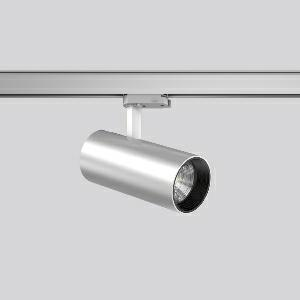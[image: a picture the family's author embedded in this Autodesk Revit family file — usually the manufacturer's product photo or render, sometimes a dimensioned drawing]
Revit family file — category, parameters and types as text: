
# Revit family: deecos_s_mini_742200_004_1_ad45
name_source: partatom
category: Lighting Fixtures
units: mm (PartAtom-declared; Revit-internal decimal feet)

## family parameters
Cut with Voids When Loaded = No
Host = Face
Light Source = No
Part Type = Normal
Room Calculation Point = No
Round Connector Dimension = Use Diameter
Shared = No

## types (1)
- DEECOS S mini (1 x LED Modul 940, 2150 lm, 4000)
    Apparent Load = 20 VA
    Approval mark = CE
    CIE Flux Codes = 98 100 100 100 100
    Color Rendering = 92
    Color Temperature = 4000
    Default Elevation = 1800 mm
    Description = Series: DEECOS S mini
LED surface-mounted projector in modern design with no visible cooling ribs. Housing: die-cast aluminium, powder-coated. Rotation range: 356°. Swivel range: 90°. Black plastic ring and recessed LED to prevent glare from the side. Optical assembly with lens made of plastic (polycarbonate) for the best homogeneous light distribution - can be changed without tools. Best colour rendering index Ra>90. With multi adaptor for 3-circuit tracks 230 V. Suitable for Track on ceiling, Wall track. High quality converter without flickering and stroboscopic effect. The following accessories can be mounted without use of tools: interchangeable lenses, decorative glasses, honeycomb louvre, clear and frosted diffusers, white interchangeable plastic ring. 
Colour: silver
Diameter: 87 mm
Height: 214 mm
Lamp: LED
Socket: without socket
Colour temperature: 4000K
Colour rendering index (CRI): 92
System power: 20 W
Rated luminous flux: 2150 lm
Luminous efficiency: 108 lm/W
Control gear: Regulated power supply
Protection class: I
Type of protection: IP 20
    Height = 214 mm
    Lamp = 1 x LED Modul 940
    Lamp Light Flux = 2150 lm
    Lamp count = 1
    Length = 87 mm
    Lifetime = 50000 h
    Luminous efficacy = 108 lm/W
    Manufacturer = RZB
    ModVariant = No
    Model = 742200.004.1
    Mounting Place = Ceiling
    Mounting Type = Rail mounted
    Number of Poles = 1
    OnlyDefault = Yes
    Power Factor = 1
    Product Name = DEECOS S mini
    Product group = Track mounted projectors
    ProductGroupID = 301
    Protection Class = Protection class I
    Protection Degree = IP 20
    RLX_Detail_Level = 1
    RLX_Emergency_Light_Flux = 0 lm
    RLX_Emergency_Type = 0
    RLX_Emergency_Type_DB = No
    RlxData = <blob elided: 37529 chars, md5=7086a62f>
    Socket = socket
    Standby Power = 0 W
    System Light Flux = 2150 lm
    System Power = 20 W
    Type Comments = Product without accessories
    Type Image = 741930.004.jpg
    URL = http://relux.com
    VarID = ---
    Voltage = 230 V
    Voltage Range = 220-240 V
    Weight = 0.00 kg
    Width = 0 mm  [stored 0 ft]

note: [stored X ft] marks values corroborated as IEEE doubles in the binary element streams (Revit-internal decimal feet)

## geometry (parser evidence)
native form markers: Blend x4, Sweep x12
no freeform markers — native parametric forms only
